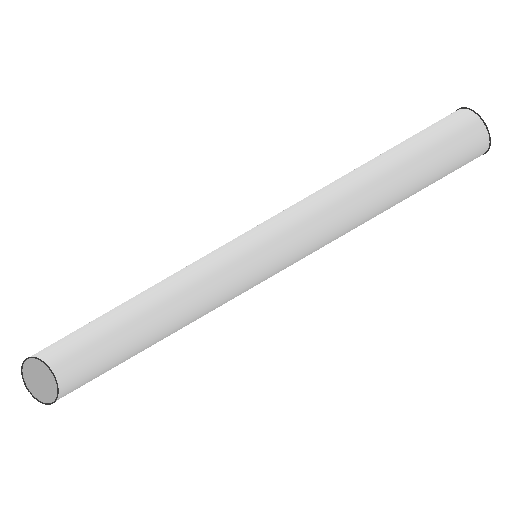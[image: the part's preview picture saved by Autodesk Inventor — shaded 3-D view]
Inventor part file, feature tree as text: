
AUTODESK INVENTOR PART (.ipt)
format: ipt  version: 2025.2 (Build 292293000, 293)  size: 84,992 bytes
history: native  units: in
note: dims shown in document units (in); Inventor stores cm internally (conversion verified against a paired STEP export)
features: extrude x1, sketch x1
ambient origin geometry x8: Origin, YZ Plane, XZ Plane, XY Plane, X Axis, Y Axis, Z Axis, Center Point
bodies: Solid1 (feature_tree)
feature tree (2):
  extrude  "Extrusion1"  Depth=3.75in TaperAngle=0.0deg
  sketch  "Sketch1"  dims[d0=0.315in d1=3.75in d2=0.0in]
